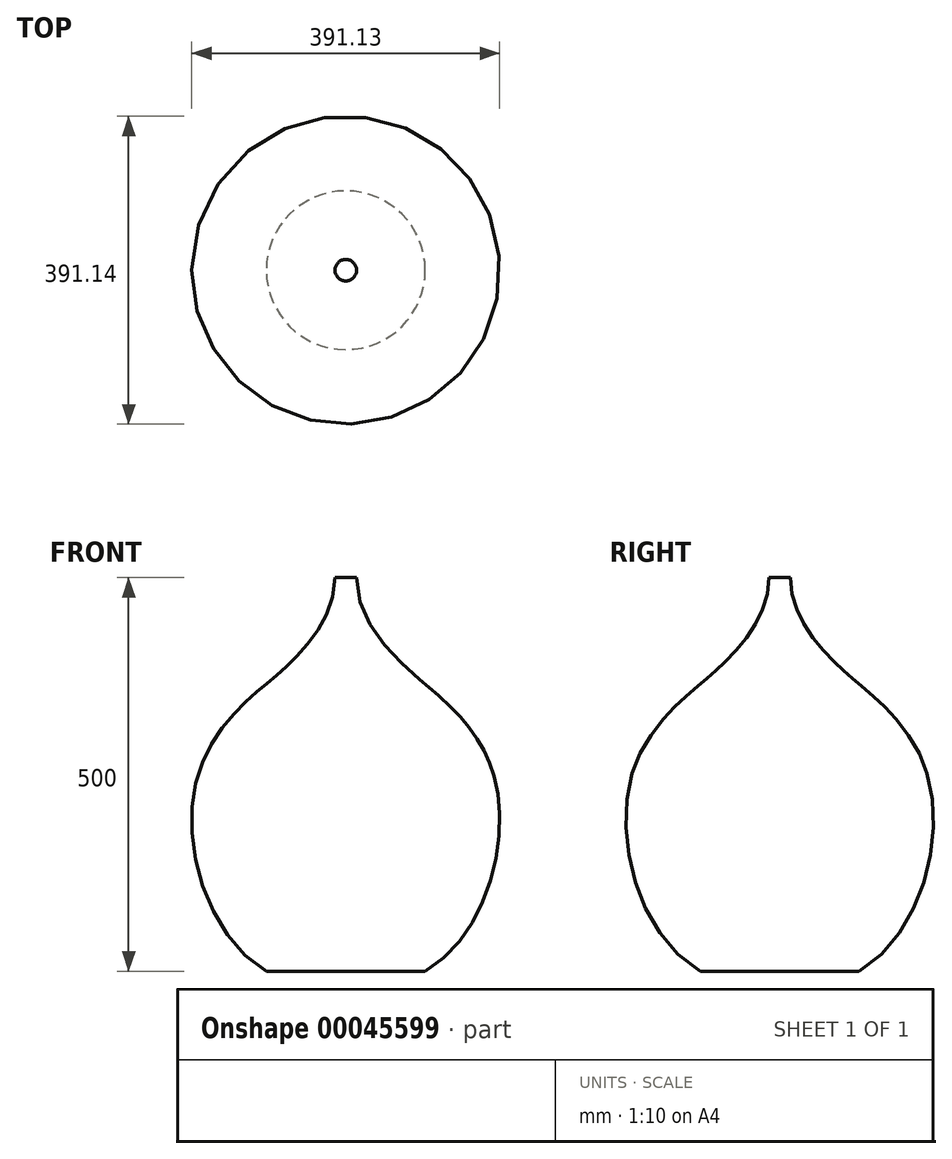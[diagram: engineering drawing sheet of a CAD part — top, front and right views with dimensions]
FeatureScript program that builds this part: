
annotation { "Feature Type Name" : "Feature", "Feature Type Description" : "" }
export const myFeature = defineFeature(function(context is Context, id is Id, definition is map)
    precondition{}
    {
        {
            var Q0;
            Q0=qCreatedBy(makeId("Front.planeOp"),FACE);
            var sketch = newSketch(context, id + "F0", { "sketchPlane" : qUnion([Q0])});
            skLineSegment(sketch, "E0", {"start": v(0, 0) * mm, "end": v(0, 500) * mm});
            skLineSegment(sketch, "E1", {"start": v(0, 500) * mm, "end": v(-13.64, 500) * mm});
            skLineSegment(sketch, "E2", {"start": v(0, 0) * mm, "end": v(-100.87, 0) * mm});
            skFitSpline(sketch, "E3", {"points": [v(-100.87, 0) * mm, v(-192.02, 232.2) * mm, v(-119.28, 349.1) * mm, v(-66.73, 395.68) * mm, v(-13.64, 500) * mm], "startDerivative": vector(-674.48, 396.8) * mm, "endDerivative": vector(0, 579.47) * mm});
            skSolve(sketch);
        }
        {
            var Q0;
            Q0=makeQuery(id+"F0.imprint","IMPRINT",FACE,{"disambiguationData":[TD([[makeQuery(id+"F0.imprint","IMPRINT",EDGE,{"derivedFrom":sQuery(id+"F0.wireOp",EDGE,"E0")}),1.0]])]});
            var Q1;
            Q1=sQuery(id+"F0.wireOp",EDGE,"E0");
            revolve(context, id + "F1", {"entities" : qUnion([Q0]), "axis" : qUnion([Q1]), "revolveType" : RevolveType.FULL});
        }
    });
